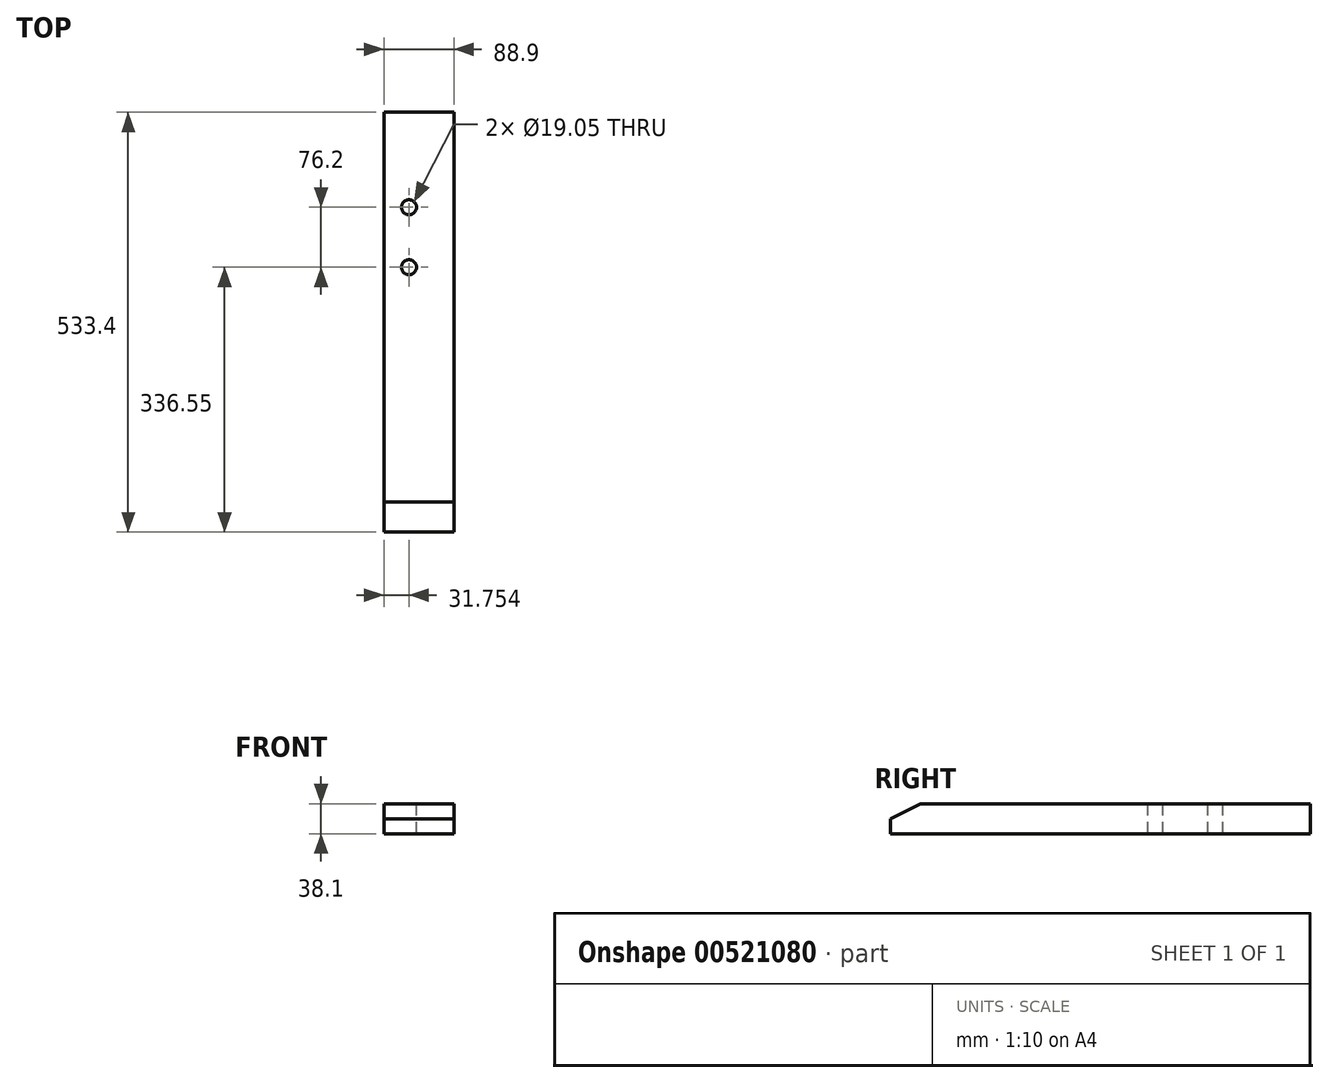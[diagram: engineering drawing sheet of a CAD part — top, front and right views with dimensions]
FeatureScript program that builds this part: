
annotation { "Feature Type Name" : "Feature", "Feature Type Description" : "" }
export const myFeature = defineFeature(function(context is Context, id is Id, definition is map)
    precondition{}
    {
        {
            var Q0;
            Q0=qCreatedBy(makeId("Front.planeOp"),FACE);
            var sketch = newSketch(context, id + "F0", { "sketchPlane" : qUnion([Q0])});
            skLineSegment(sketch, "E0.bottom", {"start": v(-42.4, -19.67) * mm, "end": v(46.5, -19.67) * mm});
            skLineSegment(sketch, "E0.top", {"start": v(-42.4, 18.43) * mm, "end": v(46.5, 18.43) * mm});
            skLineSegment(sketch, "E0.left", {"start": v(-42.4, -19.67) * mm, "end": v(-42.4, 18.43) * mm});
            skLineSegment(sketch, "E0.right", {"start": v(46.5, -19.67) * mm, "end": v(46.5, 18.43) * mm});
            skLineSegment(sketch, "E1", {"start": v(0, 43.94) * mm, "end": v(0, -47.52) * mm, "construction": true});
            skLineSegment(sketch, "E2", {"start": v(-64.12, 0) * mm, "end": v(66.16, 0) * mm, "construction": true});
            skSolve(sketch);
        }
        {
            var Q0;
            Q0 = qSketchRegion(id + "F0", true);
            extrude(context, id + "F1", {"entities" : qUnion([Q0]), "endBound" : BoundingType.SYMMETRIC, "depth" : 533.4 * mm, "offsetDistance" : 25.4 * mm});
        }
        {
            var Q0;
            Q0=makeQuery(id+"F1.opExtrude","SWEPT_FACE",FACE,{"disambiguationData":[OSD([sQuery(id+"F0.wireOp",EDGE,"E0.right")])]});
            var sketch = newSketch(context, id + "F2", { "sketchPlane" : qUnion([Q0])});
            skLineSegment(sketch, "E3.0.0", {"start": v(266.7, -19.67) * mm, "end": v(266.7, 18.43) * mm});
            skLineSegment(sketch, "E3.0.1", {"start": v(266.7, 18.43) * mm, "end": v(-266.7, 18.43) * mm});
            skLineSegment(sketch, "E3.0.2", {"start": v(-266.7, 18.43) * mm, "end": v(-266.7, -19.67) * mm});
            skLineSegment(sketch, "E3.0.3", {"start": v(-266.7, -19.67) * mm, "end": v(266.7, -19.67) * mm});
            skLineSegment(sketch, "E4", {"start": v(-266.7, -0.62) * mm, "end": v(-228.6, 18.43) * mm});
            skSolve(sketch);
        }
        {
            var Q0;
            {var subQ3=sQuery(id+"F2.wireOp",EDGE,"E4");Q0=makeQuery(id+"F2.imprint","IMPRINT",FACE,{"disambiguationData":[TD([[makeQuery(id+"F2.imprint","IMPRINT",EDGE,{"derivedFrom":subQ3}),1.0]])]});}
            extrude(context, id + "F3", {"entities" : qUnion([Q0]), "operationType" : NewBodyOperationType.REMOVE, "endBound" : BoundingType.THROUGH_ALL, "oppositeDirection" : true, "depth" : 25.4 * mm, "offsetDistance" : 25.4 * mm});
        }
        {
            var Q0;
            Q0=makeQuery(id+"F1.opExtrude","SWEPT_FACE",FACE,{"disambiguationData":[OSD([sQuery(id+"F0.wireOp",EDGE,"E0.top")])]});
            var sketch = newSketch(context, id + "F4", { "sketchPlane" : qUnion([Q0])});
            skLineSegment(sketch, "E5", {"start": v(-10.66, 266.7) * mm, "end": v(-10.66, -228.6) * mm, "construction": true});
            skCircle(sketch, "E6", {"center": v(-10.66, 146.05) * mm, "radius": 9.52 * mm});
            skCircle(sketch, "E7", {"center": v(-10.66, 69.85) * mm, "radius": 9.52 * mm});
            skSolve(sketch);
        }
        {
            var Q0;
            Q0=makeQuery(id+"F4.imprint","IMPRINT",FACE,{"disambiguationData":[TD([[makeQuery(id+"F4.imprint","IMPRINT",EDGE,{"derivedFrom":sQuery(id+"F4.wireOp",EDGE,"E6")}),1.0]])]});
            var Q1;
            Q1=makeQuery(id+"F4.imprint","IMPRINT",FACE,{"disambiguationData":[TD([[makeQuery(id+"F4.imprint","IMPRINT",EDGE,{"derivedFrom":sQuery(id+"F4.wireOp",EDGE,"E7")}),1.0]])]});
            extrude(context, id + "F5", {"entities" : qUnion([Q0, Q1]), "operationType" : NewBodyOperationType.REMOVE, "endBound" : BoundingType.THROUGH_ALL, "oppositeDirection" : true, "depth" : 25.4 * mm, "offsetDistance" : 25.4 * mm});
        }
    });
